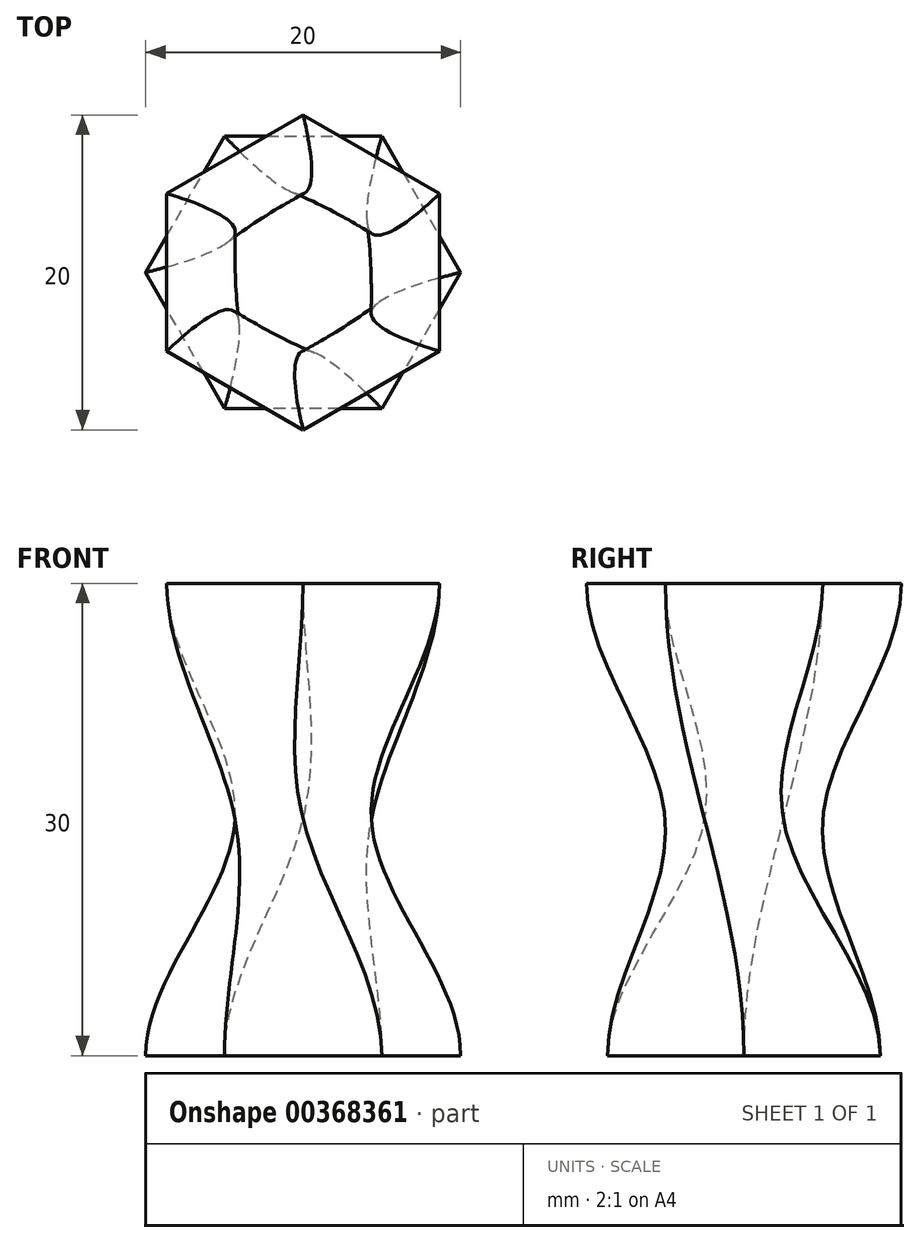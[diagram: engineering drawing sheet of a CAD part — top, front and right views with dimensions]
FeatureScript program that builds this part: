
annotation { "Feature Type Name" : "Feature", "Feature Type Description" : "" }
export const myFeature = defineFeature(function(context is Context, id is Id, definition is map)
    precondition{}
    {
        {
            var Q0;
            Q0=qCreatedBy(makeId("Top.planeOp"),FACE);
            var sketch = newSketch(context, id + "F0", { "sketchPlane" : qUnion([Q0])});
            skCircle(sketch, "E0.cCircle", {"center": v(0, 0) * mm, "radius": 10 * mm, "construction": true});
            skLineSegment(sketch, "E0.0", {"start": v(10, 0) * mm, "end": v(5, -8.66) * mm});
            skLineSegment(sketch, "E0.1", {"start": v(5, -8.66) * mm, "end": v(-5, -8.66) * mm});
            skLineSegment(sketch, "E0.2", {"start": v(-5, -8.66) * mm, "end": v(-10, 0) * mm});
            skLineSegment(sketch, "E0.3", {"start": v(-10, 0) * mm, "end": v(-5, 8.66) * mm});
            skLineSegment(sketch, "E0.4", {"start": v(-5, 8.66) * mm, "end": v(5, 8.66) * mm});
            skLineSegment(sketch, "E0.5", {"start": v(5, 8.66) * mm, "end": v(10, 0) * mm});
            skSolve(sketch);
        }
        {
            var Q0;
            Q0=qCreatedBy(makeId("Top.planeOp"),FACE);
            cPlane(context, id + "F1", {"entities" : qUnion([Q0]), "cplaneType" : CPlaneType.OFFSET, "offset" : 15 * mm, "width" : 150 * mm, "height" : 150 * mm});
        }
        {
            var Q0;
            Q0=qCreatedBy(id+"F1.planeOp",FACE);
            var sketch = newSketch(context, id + "F2", { "sketchPlane" : qUnion([Q0])});
            skCircle(sketch, "E1.cCircle", {"center": v(0, 0) * mm, "radius": 5 * mm, "construction": true});
            skLineSegment(sketch, "E1.0", {"start": v(-4.33, -2.5) * mm, "end": v(-4.33, 2.5) * mm});
            skLineSegment(sketch, "E1.1", {"start": v(-4.33, 2.5) * mm, "end": v(0, 5) * mm});
            skLineSegment(sketch, "E1.2", {"start": v(0, 5) * mm, "end": v(4.33, 2.5) * mm});
            skLineSegment(sketch, "E1.3", {"start": v(4.33, 2.5) * mm, "end": v(4.33, -2.5) * mm});
            skLineSegment(sketch, "E1.4", {"start": v(4.33, -2.5) * mm, "end": v(0, -5) * mm});
            skLineSegment(sketch, "E1.5", {"start": v(0, -5) * mm, "end": v(-4.33, -2.5) * mm});
            skSolve(sketch);
        }
        {
            var Q0;
            Q0=qCreatedBy(id+"F1.planeOp",FACE);
            cPlane(context, id + "F3", {"entities" : qUnion([Q0]), "cplaneType" : CPlaneType.OFFSET, "offset" : 15 * mm, "width" : 150 * mm, "height" : 150 * mm});
        }
        {
            var Q0;
            Q0=qCreatedBy(id+"F3.planeOp",FACE);
            var sketch = newSketch(context, id + "F4", { "sketchPlane" : qUnion([Q0])});
            skCircle(sketch, "E2.cCircle", {"center": v(0, 0) * mm, "radius": 10 * mm, "construction": true});
            skLineSegment(sketch, "E2.0", {"start": v(-8.66, -5) * mm, "end": v(-8.66, 5) * mm});
            skLineSegment(sketch, "E2.1", {"start": v(-8.66, 5) * mm, "end": v(0, 10) * mm});
            skLineSegment(sketch, "E2.2", {"start": v(0, 10) * mm, "end": v(8.66, 5) * mm});
            skLineSegment(sketch, "E2.3", {"start": v(8.66, 5) * mm, "end": v(8.66, -5) * mm});
            skLineSegment(sketch, "E2.4", {"start": v(8.66, -5) * mm, "end": v(0, -10) * mm});
            skLineSegment(sketch, "E2.5", {"start": v(0, -10) * mm, "end": v(-8.66, -5) * mm});
            skSolve(sketch);
        }
        {
            var Q0;
            Q0=makeQuery(id+"F0.imprint","IMPRINT",FACE,{"disambiguationData":[TD([[makeQuery(id+"F0.imprint","IMPRINT",EDGE,{"derivedFrom":sQuery(id+"F0.wireOp",EDGE,"E0.0")}),-1.0]])]});
            var Q1;
            Q1=makeQuery(id+"F2.imprint","IMPRINT",FACE,{"disambiguationData":[TD([[makeQuery(id+"F2.imprint","IMPRINT",EDGE,{"derivedFrom":sQuery(id+"F2.wireOp",EDGE,"E1.0")}),-1.0]])]});
            var Q2;
            Q2=makeQuery(id+"F4.imprint","IMPRINT",FACE,{"disambiguationData":[TD([[makeQuery(id+"F4.imprint","IMPRINT",EDGE,{"derivedFrom":sQuery(id+"F4.wireOp",EDGE,"E2.0")}),-1.0]])]});
            var Q3;
            Q3=makeQuery(id+"F0.imprint","IMPRINT",FACE,{"disambiguationData":[TD([[makeQuery(id+"F0.imprint","IMPRINT",EDGE,{"derivedFrom":sQuery(id+"F0.wireOp",EDGE,"E0.0")}),-1.0]])]});
            var Q4;
            Q4=makeQuery(id+"F2.imprint","IMPRINT",FACE,{"disambiguationData":[TD([[makeQuery(id+"F2.imprint","IMPRINT",EDGE,{"derivedFrom":sQuery(id+"F2.wireOp",EDGE,"E1.0")}),-1.0]])]});
            var Q5;
            Q5=makeQuery(id+"F4.imprint","IMPRINT",FACE,{"disambiguationData":[TD([[makeQuery(id+"F4.imprint","IMPRINT",EDGE,{"derivedFrom":sQuery(id+"F4.wireOp",EDGE,"E2.0")}),-1.0]])]});
            loft(context, id + "F5", {"bodyType" : ToolBodyType.SURFACE, "startCondition" : LoftEndDerivativeType.NORMAL_TO_PROFILE, "startMagnitude" : 1, "endCondition" : LoftEndDerivativeType.NORMAL_TO_PROFILE, "endMagnitude" : 1, "sheetProfilesArray" : [{ "sheetProfileEntities" : qUnion([Q0]) }, { "sheetProfileEntities" : qUnion([Q1]) }, { "sheetProfileEntities" : qUnion([Q2]) }], "wireProfilesArray" : [{ "wireProfileEntities" : qUnion([Q3]) }, { "wireProfileEntities" : qUnion([Q4]) }, { "wireProfileEntities" : qUnion([Q5]) }]});
        }
    });
